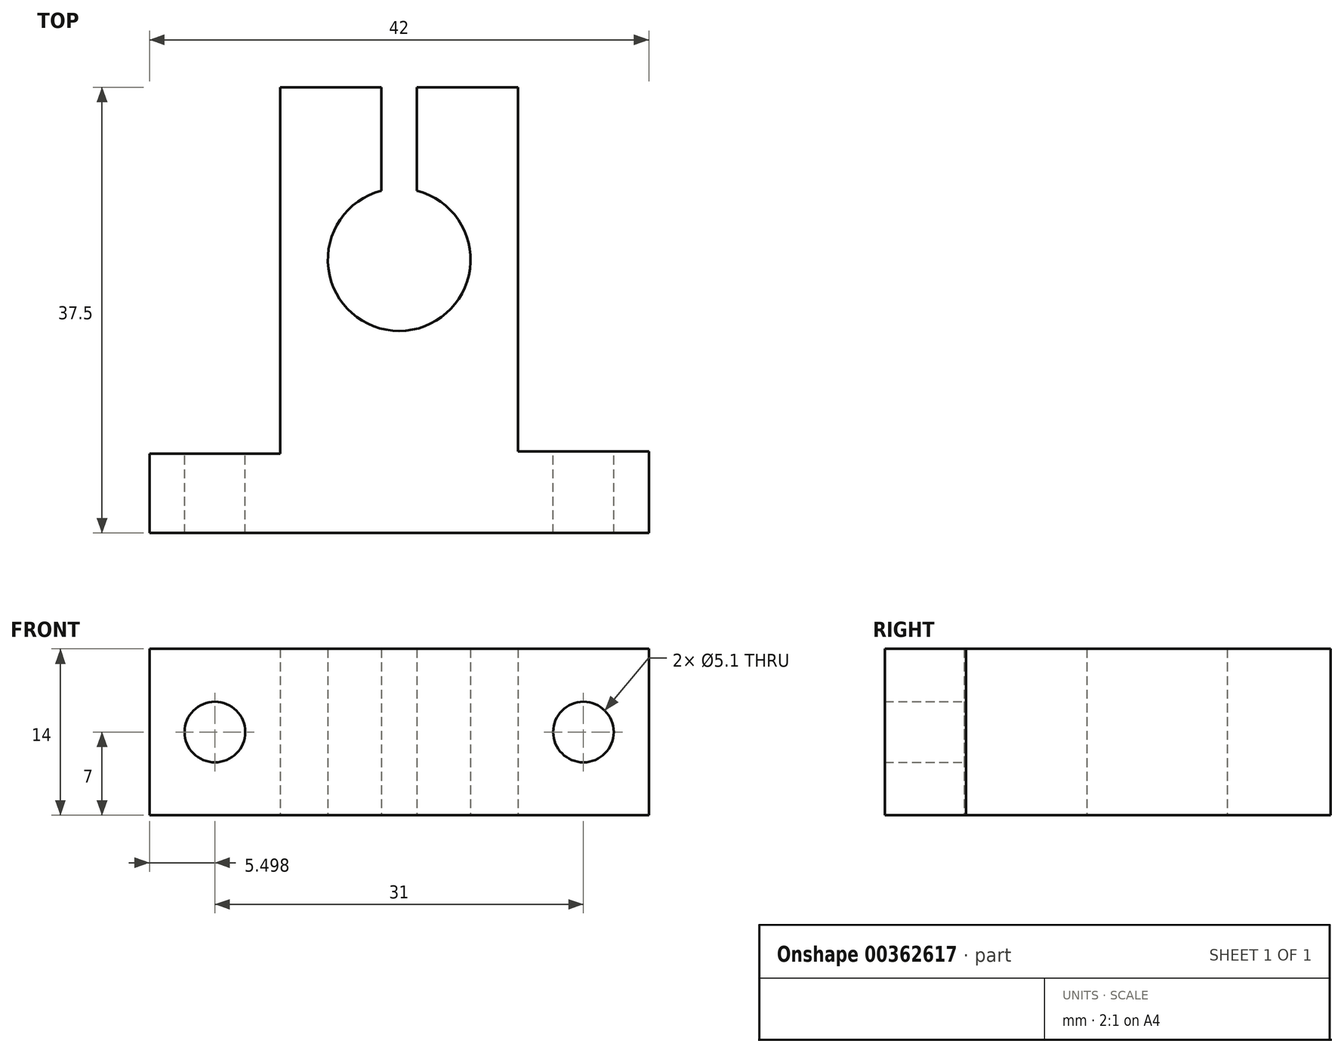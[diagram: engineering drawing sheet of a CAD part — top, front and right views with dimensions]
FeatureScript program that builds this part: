
annotation { "Feature Type Name" : "Feature", "Feature Type Description" : "" }
export const myFeature = defineFeature(function(context is Context, id is Id, definition is map)
    precondition{}
    {
        {
            var Q0;
            Q0=qCreatedBy(makeId("Top.planeOp"),FACE);
            var sketch = newSketch(context, id + "F0", { "sketchPlane" : qUnion([Q0])});
            skLineSegment(sketch, "E0", {"start": v(-68.45, 0) * mm, "end": v(-68.45, 6.68) * mm});
            skLineSegment(sketch, "E1", {"start": v(-68.45, 6.68) * mm, "end": v(-57.45, 6.68) * mm});
            skLineSegment(sketch, "E2", {"start": v(-57.45, 6.68) * mm, "end": v(-57.45, 37.5) * mm});
            skLineSegment(sketch, "E3", {"start": v(-57.45, 37.5) * mm, "end": v(-48.95, 37.5) * mm});
            skLineSegment(sketch, "E4", {"start": v(-48.95, 37.5) * mm, "end": v(-48.95, 28.8) * mm});
            skLineSegment(sketch, "E5", {"start": v(-45.95, 28.8) * mm, "end": v(-45.95, 37.5) * mm});
            skLineSegment(sketch, "E6", {"start": v(-45.95, 37.5) * mm, "end": v(-37.45, 37.5) * mm});
            skLineSegment(sketch, "E7", {"start": v(-37.45, 37.5) * mm, "end": v(-37.45, 6.85) * mm});
            skLineSegment(sketch, "E8", {"start": v(-37.45, 6.85) * mm, "end": v(-26.45, 6.85) * mm});
            skLineSegment(sketch, "E9", {"start": v(-26.45, 6.85) * mm, "end": v(-26.45, 0) * mm});
            skLineSegment(sketch, "E10", {"start": v(-26.45, 0) * mm, "end": v(-68.45, 0) * mm});
            skLineSegment(sketch, "E11", {"start": v(-47.45, 37.5) * mm, "end": v(-47.45, 11.68) * mm, "construction": true});
            skLineSegment(sketch, "E12", {"start": v(-58.27, 23) * mm, "end": v(-22.6, 23) * mm, "construction": true});
            skPoint(sketch, "E13", {"position": v(-47.45, 23) * mm});
            skArc(sketch, "E14", {"start": v(-48.95, 28.8) * mm, "mid": v(-47.45, 17) * mm, "end": v(-45.95, 28.8) * mm});
            skPoint(sketch, "E15", {"position": v(-45.95, 28.8) * mm});
            skPoint(sketch, "E16", {"position": v(-48.95, 28.8) * mm});
            skSolve(sketch);
        }
        {
            var Q0;
            Q0 = qSketchRegion(id + "F0", true);
            extrude(context, id + "F1", {"entities" : qUnion([Q0]), "depth" : 14 * mm});
        }
        {
            var Q0;
            Q0=makeQuery(id+"F1.opExtrude","SWEPT_FACE",FACE,{"disambiguationData":[OSD([sQuery(id+"F0.wireOp",EDGE,"E10")])]});
            var sketch = newSketch(context, id + "F2", { "sketchPlane" : qUnion([Q0])});
            skPoint(sketch, "E17.0", {"position": v(-57.45, 14) * mm});
            skPoint(sketch, "E17.1", {"position": v(-68.45, 14) * mm});
            skPoint(sketch, "E17.2", {"position": v(-37.45, 14) * mm});
            skPoint(sketch, "E17.3", {"position": v(-26.45, 14) * mm});
            skLineSegment(sketch, "E18", {"start": v(-37.45, 14) * mm, "end": v(-26.45, 14) * mm, "construction": true});
            skLineSegment(sketch, "E19", {"start": v(-68.45, 14) * mm, "end": v(-57.45, 14) * mm, "construction": true});
            skPoint(sketch, "E20", {"position": v(-62.95, 14) * mm});
            skPoint(sketch, "E21", {"position": v(-31.95, 14) * mm});
            skLineSegment(sketch, "E22", {"start": v(-31.95, 14) * mm, "end": v(-31.95, 0) * mm, "construction": true});
            skLineSegment(sketch, "E23", {"start": v(-62.95, 14) * mm, "end": v(-62.95, 0) * mm, "construction": true});
            skLineSegment(sketch, "E24", {"start": v(-68.45, 7) * mm, "end": v(-26.45, 7) * mm, "construction": true});
            skPoint(sketch, "E25", {"position": v(-62.95, 7) * mm});
            skPoint(sketch, "E26", {"position": v(-31.95, 7) * mm});
            skSolve(sketch);
        }
        {
            var Q0;
            Q0=sQuery(id+"F2.wireOp",VERTEX,"E25");
            var Q1;
            Q1=sQuery(id+"F2.wireOp",VERTEX,"E26");
            var Q2;
            Q2=makeQuery(id+"F1.opExtrude","SWEPT_BODY",BODY,{"disambiguationData":[OSD([sQuery(id+"F0.wireOp",EDGE,"E0"),sQuery(id+"F0.wireOp",EDGE,"E1"),sQuery(id+"F0.wireOp",EDGE,"E2"),sQuery(id+"F0.wireOp",EDGE,"E3"),sQuery(id+"F0.wireOp",EDGE,"E4"),sQuery(id+"F0.wireOp",EDGE,"E5"),sQuery(id+"F0.wireOp",EDGE,"E6"),sQuery(id+"F0.wireOp",EDGE,"E7"),sQuery(id+"F0.wireOp",EDGE,"E8"),sQuery(id+"F0.wireOp",EDGE,"E9"),sQuery(id+"F0.wireOp",EDGE,"E10"),sQuery(id+"F0.wireOp",EDGE,"E14")])]});
            hole(context, id + "F3", {"style" : HoleStyle.SIMPLE, "endStyle" : HoleEndStyle.THROUGH, "holeDiameter" : 5.1 * mm, "isTappedThrough" : true, "tappedDepth" : 12 * mm, "tapClearance" : 3, "locations" : qUnion([Q0, Q1]), "scope" : qUnion([Q2]), "startStyle" : HoleStartStyle.PART});
        }
    });
